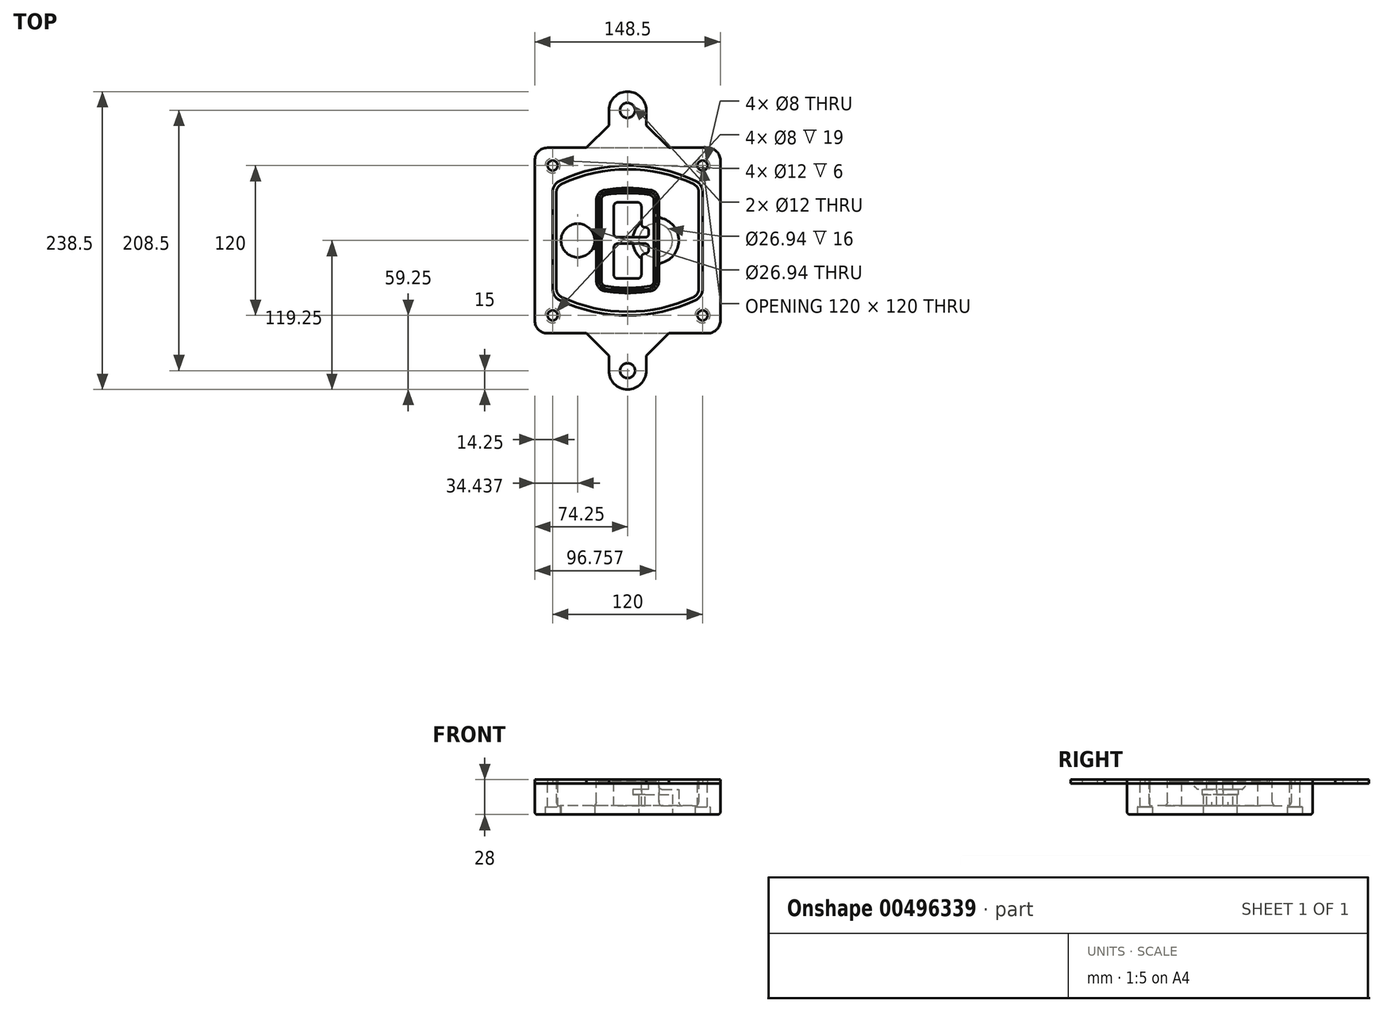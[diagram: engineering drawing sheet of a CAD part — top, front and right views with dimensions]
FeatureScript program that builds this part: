
annotation { "Feature Type Name" : "Feature", "Feature Type Description" : "" }
export const myFeature = defineFeature(function(context is Context, id is Id, definition is map)
    precondition{}
    {
        {
            var Q0;
            Q0=qCreatedBy(makeId("Top.planeOp"),FACE);
            var sketch = newSketch(context, id + "F0", { "sketchPlane" : qUnion([Q0])});
            skPoint(sketch, "E0.rect.middle", {"position": v(0, 0) * mm});
            skLineSegment(sketch, "E1.bottom", {"start": v(-64.25, -74.25) * mm, "end": v(64.25, -74.25) * mm});
            skLineSegment(sketch, "E1.top", {"start": v(-64.25, 74.25) * mm, "end": v(64.25, 74.25) * mm});
            skLineSegment(sketch, "E1.left", {"start": v(-74.25, -64.25) * mm, "end": v(-74.25, 64.25) * mm});
            skLineSegment(sketch, "E1.right", {"start": v(74.25, -64.25) * mm, "end": v(74.25, 64.25) * mm});
            skLineSegment(sketch, "E2", {"start": v(-74.25, 74.25) * mm, "end": v(74.25, -74.25) * mm, "construction": true});
            skLineSegment(sketch, "E3", {"start": v(74.25, 74.25) * mm, "end": v(-74.25, -74.25) * mm, "construction": true});
            skCircle(sketch, "E4", {"center": v(-60, 60) * mm, "radius": 4 * mm});
            skCircle(sketch, "E5", {"center": v(60, 60) * mm, "radius": 4 * mm});
            skCircle(sketch, "E6", {"center": v(60, -60) * mm, "radius": 4 * mm});
            skCircle(sketch, "E7", {"center": v(-60, -60) * mm, "radius": 4 * mm});
            skLineSegment(sketch, "E8", {"start": v(-60, 60) * mm, "end": v(60, 60) * mm, "construction": true});
            skLineSegment(sketch, "E9", {"start": v(60, 60) * mm, "end": v(60, -60) * mm, "construction": true});
            skLineSegment(sketch, "E10", {"start": v(60, -60) * mm, "end": v(-60, -60) * mm, "construction": true});
            skLineSegment(sketch, "E11", {"start": v(-60, -60) * mm, "end": v(-60, 60) * mm, "construction": true});
            skLineSegment(sketch, "E12", {"start": v(-60, 38.83) * mm, "end": v(-60, -38.83) * mm});
            skLineSegment(sketch, "E13", {"start": v(60, 38.83) * mm, "end": v(60, -38.83) * mm});
            skArc(sketch, "E14", {"start": v(54.26, 47.88) * mm, "mid": v(0, 60) * mm, "end": v(-54.26, 47.88) * mm});
            skArc(sketch, "E15", {"start": v(-54.26, -47.88) * mm, "mid": v(0, -60) * mm, "end": v(54.26, -47.88) * mm});
            skLineSegment(sketch, "E16", {"start": v(-60, 0) * mm, "end": v(60, 0) * mm, "construction": true});
            skPoint(sketch, "E17.visualSharp", {"position": v(-60, -45) * mm});
            skArc(sketch, "E17.filletArc", {"start": v(-60, -38.83) * mm, "mid": v(-58.44, -44.2) * mm, "end": v(-54.26, -47.88) * mm});
            skPoint(sketch, "E18.visualSharp", {"position": v(-60, 45) * mm});
            skArc(sketch, "E18.filletArc", {"start": v(-54.26, 47.88) * mm, "mid": v(-58.44, 44.2) * mm, "end": v(-60, 38.83) * mm});
            skPoint(sketch, "E19.visualSharp", {"position": v(60, 45) * mm});
            skArc(sketch, "E19.filletArc", {"start": v(60, 38.83) * mm, "mid": v(58.44, 44.2) * mm, "end": v(54.26, 47.88) * mm});
            skPoint(sketch, "E20.visualSharp", {"position": v(60, -45) * mm});
            skArc(sketch, "E20.filletArc", {"start": v(54.26, -47.88) * mm, "mid": v(58.44, -44.2) * mm, "end": v(60, -38.83) * mm});
            skPoint(sketch, "E21.visualSharp", {"position": v(-74.25, 74.25) * mm});
            skArc(sketch, "E21.filletArc", {"start": v(-64.25, 74.25) * mm, "mid": v(-71.32, 71.32) * mm, "end": v(-74.25, 64.25) * mm});
            skPoint(sketch, "E22.visualSharp", {"position": v(74.25, 74.25) * mm});
            skArc(sketch, "E22.filletArc", {"start": v(74.25, 64.25) * mm, "mid": v(71.32, 71.32) * mm, "end": v(64.25, 74.25) * mm});
            skPoint(sketch, "E23.visualSharp", {"position": v(74.25, -74.25) * mm});
            skArc(sketch, "E23.filletArc", {"start": v(64.25, -74.25) * mm, "mid": v(71.32, -71.32) * mm, "end": v(74.25, -64.25) * mm});
            skPoint(sketch, "E24.visualSharp", {"position": v(-74.25, -74.25) * mm});
            skArc(sketch, "E24.filletArc", {"start": v(-74.25, -64.25) * mm, "mid": v(-71.32, -71.32) * mm, "end": v(-64.25, -74.25) * mm});
            skArc(sketch, "E25.0", {"start": v(57, 38.83) * mm, "mid": v(55.9, 42.58) * mm, "end": v(52.98, 45.17) * mm});
            skLineSegment(sketch, "E25.1", {"start": v(57, 38.83) * mm, "end": v(57, -38.83) * mm});
            skArc(sketch, "E25.2", {"start": v(52.98, -45.17) * mm, "mid": v(55.9, -42.58) * mm, "end": v(57, -38.83) * mm});
            skArc(sketch, "E25.3", {"start": v(-52.98, -45.17) * mm, "mid": v(0, -57) * mm, "end": v(52.98, -45.17) * mm});
            skArc(sketch, "E25.4", {"start": v(-57, -38.83) * mm, "mid": v(-55.9, -42.58) * mm, "end": v(-52.98, -45.17) * mm});
            skArc(sketch, "E25.5", {"start": v(52.98, 45.17) * mm, "mid": v(0, 57) * mm, "end": v(-52.98, 45.17) * mm});
            skLineSegment(sketch, "E25.6", {"start": v(-57, 38.83) * mm, "end": v(-57, -38.83) * mm});
            skArc(sketch, "E25.7", {"start": v(-52.98, 45.17) * mm, "mid": v(-55.9, 42.58) * mm, "end": v(-57, 38.83) * mm});
            skArc(sketch, "E26.0", {"start": v(-55.96, 51.5) * mm, "mid": v(-61.82, 46.33) * mm, "end": v(-64, 38.83) * mm});
            skArc(sketch, "E26.1", {"start": v(55.96, 51.5) * mm, "mid": v(0, 64) * mm, "end": v(-55.96, 51.5) * mm});
            skArc(sketch, "E26.2", {"start": v(64, 38.83) * mm, "mid": v(61.82, 46.33) * mm, "end": v(55.96, 51.5) * mm});
            skLineSegment(sketch, "E26.3", {"start": v(64, 38.83) * mm, "end": v(64, -38.83) * mm});
            skArc(sketch, "E26.4", {"start": v(55.96, -51.5) * mm, "mid": v(61.82, -46.33) * mm, "end": v(64, -38.83) * mm});
            skLineSegment(sketch, "E26.5", {"start": v(-64, 38.83) * mm, "end": v(-64, -38.83) * mm});
            skArc(sketch, "E26.6", {"start": v(-55.96, -51.5) * mm, "mid": v(0, -64) * mm, "end": v(55.96, -51.5) * mm});
            skArc(sketch, "E26.7", {"start": v(-64, -38.83) * mm, "mid": v(-61.82, -46.33) * mm, "end": v(-55.96, -51.5) * mm});
            skSolve(sketch);
        }
        {
            var Q0;
            Q0=makeQuery(id+"F0.imprint","IMPRINT",FACE,{"disambiguationData":[TD([[makeQuery(id+"F0.imprint","IMPRINT",EDGE,{"derivedFrom":sQuery(id+"F0.wireOp",EDGE,"E1.bottom")}),1.0]])]});
            var Q1;
            Q1=makeQuery(id+"F0.imprint","IMPRINT",FACE,{"disambiguationData":[TD([[makeQuery(id+"F0.imprint","IMPRINT",EDGE,{"derivedFrom":sQuery(id+"F0.wireOp",EDGE,"E12")}),1.0]])]});
            var Q2;
            Q2=makeQuery(id+"F0.imprint","IMPRINT",FACE,{"disambiguationData":[TD([[makeQuery(id+"F0.imprint","IMPRINT",EDGE,{"derivedFrom":sQuery(id+"F0.wireOp",EDGE,"E25.0")}),1.0]])]});
            var Q3;
            Q3=makeQuery(id+"F0.imprint","IMPRINT",FACE,{"disambiguationData":[TD([[makeQuery(id+"F0.imprint","IMPRINT",EDGE,{"derivedFrom":sQuery(id+"F0.wireOp",EDGE,"E12")}),-1.0]])]});
            extrude(context, id + "F1", {"entities" : qUnion([Q0, Q1, Q2, Q3]), "oppositeDirection" : true, "depth" : 25 * mm});
        }
        {
            var Q0;
            Q0=makeQuery(id+"F0.imprint","IMPRINT",FACE,{"disambiguationData":[TD([[makeQuery(id+"F0.imprint","IMPRINT",EDGE,{"derivedFrom":sQuery(id+"F0.wireOp",EDGE,"E12")}),1.0]])]});
            extrude(context, id + "F2", {"entities" : qUnion([Q0]), "operationType" : NewBodyOperationType.ADD, "depth" : 3 * mm});
        }
        {
            var Q0;
            Q0=makeQuery(id+"F0.imprint","IMPRINT",FACE,{"disambiguationData":[TD([[makeQuery(id+"F0.imprint","IMPRINT",EDGE,{"derivedFrom":sQuery(id+"F0.wireOp",EDGE,"E25.0")}),1.0]])]});
            extrude(context, id + "F3", {"entities" : qUnion([Q0]), "operationType" : NewBodyOperationType.REMOVE, "oppositeDirection" : true, "depth" : 18 * mm});
        }
        {
            var Q0;
            Q0=makeQuery(id+"F2.opExtrude","CAP_FACE",FACE,{"disambiguationData":[OSD([sQuery(id+"F0.wireOp",EDGE,"E12"),sQuery(id+"F0.wireOp",EDGE,"E13"),sQuery(id+"F0.wireOp",EDGE,"E14"),sQuery(id+"F0.wireOp",EDGE,"E15"),sQuery(id+"F0.wireOp",EDGE,"E17.filletArc"),sQuery(id+"F0.wireOp",EDGE,"E18.filletArc"),sQuery(id+"F0.wireOp",EDGE,"E19.filletArc"),sQuery(id+"F0.wireOp",EDGE,"E20.filletArc"),sQuery(id+"F0.wireOp",EDGE,"E25.0"),sQuery(id+"F0.wireOp",EDGE,"E25.1"),sQuery(id+"F0.wireOp",EDGE,"E25.2"),sQuery(id+"F0.wireOp",EDGE,"E25.3"),sQuery(id+"F0.wireOp",EDGE,"E25.4"),sQuery(id+"F0.wireOp",EDGE,"E25.5"),sQuery(id+"F0.wireOp",EDGE,"E25.6"),sQuery(id+"F0.wireOp",EDGE,"E25.7")])],"isStart":false});
            var sketch = newSketch(context, id + "F4", { "sketchPlane" : qUnion([Q0])});
            skArc(sketch, "E27.0", {"start": v(-18.34, -40.45) * mm, "mid": v(0, -42) * mm, "end": v(18.34, -40.45) * mm});
            skArc(sketch, "E28.0", {"start": v(18.34, 40.45) * mm, "mid": v(0, 42) * mm, "end": v(-18.34, 40.45) * mm});
            skLineSegment(sketch, "E29", {"start": v(-25, 32.57) * mm, "end": v(-25, -32.57) * mm});
            skLineSegment(sketch, "E30", {"start": v(25, 32.57) * mm, "end": v(25, -32.57) * mm});
            skLineSegment(sketch, "E31", {"start": v(-25, 39.1) * mm, "end": v(25, 39.1) * mm, "construction": true});
            skLineSegment(sketch, "E32", {"start": v(-25, -39.1) * mm, "end": v(25, -39.1) * mm, "construction": true});
            skPoint(sketch, "E33.visualSharp", {"position": v(-25, 39.1) * mm});
            skArc(sketch, "E33.filletArc", {"start": v(-18.34, 40.45) * mm, "mid": v(-23.11, 37.73) * mm, "end": v(-25, 32.57) * mm});
            skPoint(sketch, "E34.visualSharp", {"position": v(25, 39.1) * mm});
            skArc(sketch, "E34.filletArc", {"start": v(25, 32.57) * mm, "mid": v(23.11, 37.73) * mm, "end": v(18.34, 40.45) * mm});
            skPoint(sketch, "E35.visualSharp", {"position": v(25, -39.1) * mm});
            skArc(sketch, "E35.filletArc", {"start": v(18.34, -40.45) * mm, "mid": v(23.11, -37.73) * mm, "end": v(25, -32.57) * mm});
            skPoint(sketch, "E36.visualSharp", {"position": v(-25, -39.1) * mm});
            skArc(sketch, "E36.filletArc", {"start": v(-25, -32.57) * mm, "mid": v(-23.11, -37.73) * mm, "end": v(-18.34, -40.45) * mm});
            skArc(sketch, "E37.0", {"start": v(52.98, 45.17) * mm, "mid": v(0, 57) * mm, "end": v(-52.98, 45.17) * mm});
            skArc(sketch, "E37.1", {"start": v(-52.98, 45.17) * mm, "mid": v(-55.9, 42.58) * mm, "end": v(-57, 38.83) * mm});
            skLineSegment(sketch, "E37.2", {"start": v(-57, 38.83) * mm, "end": v(-57, -38.83) * mm});
            skArc(sketch, "E37.3", {"start": v(-57, -38.83) * mm, "mid": v(-55.9, -42.58) * mm, "end": v(-52.98, -45.17) * mm});
            skArc(sketch, "E37.4", {"start": v(-52.98, -45.17) * mm, "mid": v(0, -57) * mm, "end": v(52.98, -45.17) * mm});
            skArc(sketch, "E37.5", {"start": v(52.98, -45.17) * mm, "mid": v(55.9, -42.58) * mm, "end": v(57, -38.83) * mm});
            skLineSegment(sketch, "E37.6", {"start": v(57, 38.83) * mm, "end": v(57, -38.83) * mm});
            skArc(sketch, "E37.7", {"start": v(57, 38.83) * mm, "mid": v(55.9, 42.58) * mm, "end": v(52.98, 45.17) * mm});
            skLineSegment(sketch, "E38.0", {"start": v(23, 32.57) * mm, "end": v(23, -32.57) * mm});
            skArc(sketch, "E38.1", {"start": v(18, -38.48) * mm, "mid": v(21.58, -36.44) * mm, "end": v(23, -32.57) * mm});
            skArc(sketch, "E38.2", {"start": v(-18, -38.48) * mm, "mid": v(0, -40) * mm, "end": v(18, -38.48) * mm});
            skArc(sketch, "E38.3", {"start": v(-23, -32.57) * mm, "mid": v(-21.58, -36.44) * mm, "end": v(-18, -38.48) * mm});
            skLineSegment(sketch, "E38.4", {"start": v(-23, 32.57) * mm, "end": v(-23, -32.57) * mm});
            skArc(sketch, "E38.5", {"start": v(23, 32.57) * mm, "mid": v(21.58, 36.44) * mm, "end": v(18, 38.48) * mm});
            skArc(sketch, "E38.6", {"start": v(-18, 38.48) * mm, "mid": v(-21.58, 36.44) * mm, "end": v(-23, 32.57) * mm});
            skArc(sketch, "E38.7", {"start": v(18, 38.48) * mm, "mid": v(0, 40) * mm, "end": v(-18, 38.48) * mm});
            skArc(sketch, "E39.0", {"start": v(21, 32.57) * mm, "mid": v(20.06, 35.15) * mm, "end": v(17.67, 36.5) * mm});
            skLineSegment(sketch, "E39.1", {"start": v(21, 32.57) * mm, "end": v(21, -32.57) * mm});
            skArc(sketch, "E39.2", {"start": v(17.67, -36.5) * mm, "mid": v(20.06, -35.15) * mm, "end": v(21, -32.57) * mm});
            skArc(sketch, "E39.3", {"start": v(-17.67, -36.5) * mm, "mid": v(0, -38) * mm, "end": v(17.67, -36.5) * mm});
            skArc(sketch, "E39.4", {"start": v(-21, -32.57) * mm, "mid": v(-20.06, -35.15) * mm, "end": v(-17.67, -36.5) * mm});
            skArc(sketch, "E39.5", {"start": v(17.67, 36.5) * mm, "mid": v(0, 38) * mm, "end": v(-17.67, 36.5) * mm});
            skLineSegment(sketch, "E39.6", {"start": v(-21, 32.57) * mm, "end": v(-21, -32.57) * mm});
            skArc(sketch, "E39.7", {"start": v(-17.67, 36.5) * mm, "mid": v(-20.06, 35.15) * mm, "end": v(-21, 32.57) * mm});
            skLineSegment(sketch, "E40", {"start": v(-25, 0) * mm, "end": v(25, 0) * mm, "construction": true});
            skLineSegment(sketch, "E41", {"start": v(-11, 5.5) * mm, "end": v(-11, 27.5) * mm});
            skLineSegment(sketch, "E42", {"start": v(-8, 30.5) * mm, "end": v(8, 30.5) * mm});
            skLineSegment(sketch, "E43", {"start": v(11, 27.5) * mm, "end": v(11, 13.5) * mm});
            skLineSegment(sketch, "E44", {"start": v(14, 10.5) * mm, "end": v(14, 10.5) * mm});
            skLineSegment(sketch, "E45", {"start": v(17, 7.5) * mm, "end": v(17, 5.5) * mm});
            skLineSegment(sketch, "E46", {"start": v(14, 2.5) * mm, "end": v(-8, 2.5) * mm});
            skPoint(sketch, "E47.visualSharp", {"position": v(-11, 30.5) * mm});
            skArc(sketch, "E47.filletArc", {"start": v(-8, 30.5) * mm, "mid": v(-10.12, 29.62) * mm, "end": v(-11, 27.5) * mm});
            skPoint(sketch, "E48.visualSharp", {"position": v(11, 30.5) * mm});
            skArc(sketch, "E48.filletArc", {"start": v(11, 27.5) * mm, "mid": v(10.12, 29.62) * mm, "end": v(8, 30.5) * mm});
            skPoint(sketch, "E49.visualSharp", {"position": v(11, 10.5) * mm});
            skArc(sketch, "E49.filletArc", {"start": v(11, 13.5) * mm, "mid": v(11.88, 11.38) * mm, "end": v(14, 10.5) * mm});
            skPoint(sketch, "E50.visualSharp", {"position": v(17, 10.5) * mm});
            skArc(sketch, "E50.filletArc", {"start": v(17, 7.5) * mm, "mid": v(16.12, 9.62) * mm, "end": v(14, 10.5) * mm});
            skPoint(sketch, "E51.visualSharp", {"position": v(17, 2.5) * mm});
            skArc(sketch, "E51.filletArc", {"start": v(14, 2.5) * mm, "mid": v(16.12, 3.38) * mm, "end": v(17, 5.5) * mm});
            skPoint(sketch, "E52.visualSharp", {"position": v(-11, 2.5) * mm});
            skArc(sketch, "E52.filletArc", {"start": v(-11, 5.5) * mm, "mid": v(-10.12, 3.38) * mm, "end": v(-8, 2.5) * mm});
            skLineSegment(sketch, "E53.0.MirrorCS", {"start": v(14, -2.5) * mm, "end": v(-8, -2.5) * mm});
            skArc(sketch, "E54.0.MirrorCS", {"start": v(-11, -5.5) * mm, "mid": v(-10.12, -3.38) * mm, "end": v(-8, -2.5) * mm});
            skLineSegment(sketch, "E55.0.MirrorCS", {"start": v(-11, -5.5) * mm, "end": v(-11, -27.5) * mm});
            skArc(sketch, "E56.0.MirrorCS", {"start": v(-8, -30.5) * mm, "mid": v(-10.12, -29.62) * mm, "end": v(-11, -27.5) * mm});
            skLineSegment(sketch, "E57.0.MirrorCS", {"start": v(-8, -30.5) * mm, "end": v(8, -30.5) * mm});
            skArc(sketch, "E58.0.MirrorCS", {"start": v(11, -27.5) * mm, "mid": v(10.12, -29.62) * mm, "end": v(8, -30.5) * mm});
            skLineSegment(sketch, "E59.0.MirrorCS", {"start": v(11, -27.5) * mm, "end": v(11, -13.5) * mm});
            skArc(sketch, "E60.0.MirrorCS", {"start": v(11, -13.5) * mm, "mid": v(11.88, -11.38) * mm, "end": v(14, -10.5) * mm});
            skArc(sketch, "E61.0.MirrorCS", {"start": v(17, -7.5) * mm, "mid": v(16.12, -9.62) * mm, "end": v(14, -10.5) * mm});
            skLineSegment(sketch, "E62.0.MirrorCS", {"start": v(17, -7.5) * mm, "end": v(17, -5.5) * mm});
            skArc(sketch, "E63.0.MirrorCS", {"start": v(14, -2.5) * mm, "mid": v(16.12, -3.38) * mm, "end": v(17, -5.5) * mm});
            skSolve(sketch);
        }
        {
            var Q0;
            Q0=makeQuery(id+"F4.imprint","IMPRINT",FACE,{"disambiguationData":[TD([[makeQuery(id+"F4.imprint","IMPRINT",EDGE,{"derivedFrom":sQuery(id+"F4.wireOp",EDGE,"E27.0")}),1.0]])]});
            var Q1;
            Q1=makeQuery(id+"F4.imprint","IMPRINT",FACE,{"disambiguationData":[TD([[makeQuery(id+"F4.imprint","IMPRINT",EDGE,{"derivedFrom":sQuery(id+"F4.wireOp",EDGE,"E38.0")}),-1.0]])]});
            var Q2;
            Q2=makeQuery(id+"F4.imprint","IMPRINT",FACE,{"disambiguationData":[TD([[makeQuery(id+"F4.imprint","IMPRINT",EDGE,{"derivedFrom":sQuery(id+"F4.wireOp",EDGE,"E39.0")}),1.0]])]});
            extrude(context, id + "F5", {"entities" : qUnion([Q0, Q1, Q2]), "operationType" : NewBodyOperationType.ADD, "endBound" : BoundingType.UP_TO_NEXT, "oppositeDirection" : true, "depth" : 25 * mm});
        }
        {
            var Q0;
            Q0=makeQuery(id+"F4.imprint","IMPRINT",FACE,{"disambiguationData":[TD([[makeQuery(id+"F4.imprint","IMPRINT",EDGE,{"derivedFrom":sQuery(id+"F4.wireOp",EDGE,"E38.0")}),-1.0]])]});
            extrude(context, id + "F6", {"entities" : qUnion([Q0]), "operationType" : NewBodyOperationType.REMOVE, "oppositeDirection" : true, "depth" : 2 * mm});
        }
        {
            var Q0;
            Q0=makeQuery(id+"F1.opExtrude","CAP_FACE",FACE,{"disambiguationData":[OSD([sQuery(id+"F0.wireOp",EDGE,"E1.bottom"),sQuery(id+"F0.wireOp",EDGE,"E1.top"),sQuery(id+"F0.wireOp",EDGE,"E1.left"),sQuery(id+"F0.wireOp",EDGE,"E1.right"),sQuery(id+"F0.wireOp",EDGE,"E4"),sQuery(id+"F0.wireOp",EDGE,"E5"),sQuery(id+"F0.wireOp",EDGE,"E6"),sQuery(id+"F0.wireOp",EDGE,"E7"),sQuery(id+"F0.wireOp",EDGE,"E21.filletArc"),sQuery(id+"F0.wireOp",EDGE,"E22.filletArc"),sQuery(id+"F0.wireOp",EDGE,"E23.filletArc"),sQuery(id+"F0.wireOp",EDGE,"E24.filletArc")])],"isStart":false});
            var sketch = newSketch(context, id + "F7", { "sketchPlane" : qUnion([Q0])});
            skCircle(sketch, "E64", {"center": v(22.5, 0) * mm, "radius": 13.47 * mm});
            skCircle(sketch, "E65", {"center": v(-39.81, 0) * mm, "radius": 13.47 * mm});
            skLineSegment(sketch, "E66", {"start": v(74.25, 0) * mm, "end": v(-74.25, 0) * mm});
            skCircle(sketch, "E67", {"center": v(22.5, 0) * mm, "radius": 18.47 * mm});
            skCircle(sketch, "E68", {"center": v(60, -60) * mm, "radius": 6 * mm});
            skCircle(sketch, "E69", {"center": v(-60, -60) * mm, "radius": 6 * mm});
            skCircle(sketch, "E70", {"center": v(-60, 60) * mm, "radius": 6 * mm});
            skCircle(sketch, "E71", {"center": v(60, 60) * mm, "radius": 6 * mm});
            skSolve(sketch);
        }
        {
            var Q0;
            {var subQ1=sQuery(id+"F7.wireOp",EDGE,"E66");var subQ4=sQuery(id+"F7.wireOp",EDGE,"E64");var subQ6=makeQuery(id+"F7.imprint","INTERSECT",VERTEX,{"disambiguationData":[OD(0.0)],"derivedFrom":[subQ4,subQ1]});Q0=makeQuery(id+"F7.imprint","IMPRINT",FACE,{"disambiguationData":[TD([[makeQuery(id+"F7.imprint","IMPRINT",EDGE,{"disambiguationData":[TD([[subQ6,-1.0]])],"derivedFrom":subQ4}),-1.0]])]});}
            var Q1;
            {var subQ0=sQuery(id+"F7.wireOp",EDGE,"E66");var subQ1=sQuery(id+"F7.wireOp",EDGE,"E64");var subQ3=makeQuery(id+"F7.imprint","INTERSECT",VERTEX,{"disambiguationData":[OD(0.0)],"derivedFrom":[subQ1,subQ0]});Q1=makeQuery(id+"F7.imprint","IMPRINT",FACE,{"disambiguationData":[TD([[makeQuery(id+"F7.imprint","IMPRINT",EDGE,{"disambiguationData":[TD([[subQ3,-1.0]])],"derivedFrom":subQ1}),1.0]])]});}
            var Q2;
            {var subQ0=sQuery(id+"F7.wireOp",EDGE,"E66");var subQ1=sQuery(id+"F7.wireOp",EDGE,"E64");var subQ3=makeQuery(id+"F7.imprint","INTERSECT",VERTEX,{"disambiguationData":[OD(0.0)],"derivedFrom":[subQ1,subQ0]});Q2=makeQuery(id+"F7.imprint","IMPRINT",FACE,{"disambiguationData":[TD([[makeQuery(id+"F7.imprint","IMPRINT",EDGE,{"disambiguationData":[TD([[subQ3,1.0]])],"derivedFrom":subQ1}),1.0]])]});}
            var Q3;
            {var subQ1=sQuery(id+"F7.wireOp",EDGE,"E66");var subQ4=sQuery(id+"F7.wireOp",EDGE,"E64");var subQ6=makeQuery(id+"F7.imprint","INTERSECT",VERTEX,{"disambiguationData":[OD(0.0)],"derivedFrom":[subQ4,subQ1]});Q3=makeQuery(id+"F7.imprint","IMPRINT",FACE,{"disambiguationData":[TD([[makeQuery(id+"F7.imprint","IMPRINT",EDGE,{"disambiguationData":[TD([[subQ6,1.0]])],"derivedFrom":subQ4}),-1.0]])]});}
            extrude(context, id + "F8", {"entities" : qUnion([Q0, Q1, Q2, Q3]), "operationType" : NewBodyOperationType.ADD, "oppositeDirection" : true, "depth" : 20 * mm});
        }
        {
            var Q0;
            {var subQ0=sQuery(id+"F7.wireOp",EDGE,"E66");var subQ1=sQuery(id+"F7.wireOp",EDGE,"E64");var subQ3=makeQuery(id+"F7.imprint","INTERSECT",VERTEX,{"disambiguationData":[OD(0.0)],"derivedFrom":[subQ1,subQ0]});Q0=makeQuery(id+"F7.imprint","IMPRINT",FACE,{"disambiguationData":[TD([[makeQuery(id+"F7.imprint","IMPRINT",EDGE,{"disambiguationData":[TD([[subQ3,-1.0]])],"derivedFrom":subQ1}),1.0]])]});}
            var Q1;
            {var subQ0=sQuery(id+"F7.wireOp",EDGE,"E66");var subQ1=sQuery(id+"F7.wireOp",EDGE,"E64");var subQ3=makeQuery(id+"F7.imprint","INTERSECT",VERTEX,{"disambiguationData":[OD(0.0)],"derivedFrom":[subQ1,subQ0]});Q1=makeQuery(id+"F7.imprint","IMPRINT",FACE,{"disambiguationData":[TD([[makeQuery(id+"F7.imprint","IMPRINT",EDGE,{"disambiguationData":[TD([[subQ3,1.0]])],"derivedFrom":subQ1}),1.0]])]});}
            extrude(context, id + "F9", {"entities" : qUnion([Q0, Q1]), "operationType" : NewBodyOperationType.REMOVE, "oppositeDirection" : true, "depth" : 16 * mm});
        }
        {
            var Q0;
            {var subQ0=sQuery(id+"F7.wireOp",EDGE,"E66");var subQ1=sQuery(id+"F7.wireOp",EDGE,"E65");var subQ3=makeQuery(id+"F7.imprint","INTERSECT",VERTEX,{"disambiguationData":[OD(0.0)],"derivedFrom":[subQ1,subQ0]});Q0=makeQuery(id+"F7.imprint","IMPRINT",FACE,{"disambiguationData":[TD([[makeQuery(id+"F7.imprint","IMPRINT",EDGE,{"disambiguationData":[TD([[subQ3,-1.0]])],"derivedFrom":subQ1}),1.0]])]});}
            var Q1;
            {var subQ0=sQuery(id+"F7.wireOp",EDGE,"E66");var subQ1=sQuery(id+"F7.wireOp",EDGE,"E65");var subQ3=makeQuery(id+"F7.imprint","INTERSECT",VERTEX,{"disambiguationData":[OD(0.0)],"derivedFrom":[subQ1,subQ0]});Q1=makeQuery(id+"F7.imprint","IMPRINT",FACE,{"disambiguationData":[TD([[makeQuery(id+"F7.imprint","IMPRINT",EDGE,{"disambiguationData":[TD([[subQ3,1.0]])],"derivedFrom":subQ1}),1.0]])]});}
            extrude(context, id + "F10", {"entities" : qUnion([Q0, Q1]), "operationType" : NewBodyOperationType.REMOVE, "oppositeDirection" : true, "depth" : 25 * mm});
        }
        {
            var Q0;
            Q0=makeQuery(id+"F7.imprint","IMPRINT",FACE,{"disambiguationData":[TD([[makeQuery(id+"F7.imprint","IMPRINT",EDGE,{"derivedFrom":sQuery(id+"F7.wireOp",EDGE,"E68")}),1.0]])]});
            var Q1;
            Q1=makeQuery(id+"F7.imprint","IMPRINT",FACE,{"disambiguationData":[TD([[makeQuery(id+"F7.imprint","IMPRINT",EDGE,{"derivedFrom":makeQuery(id+"F1.opExtrude","CAP_EDGE",EDGE,{"disambiguationData":[OSD([sQuery(id+"F0.wireOp",EDGE,"E5")])],"isStart":false})}),-1.0]])]});
            var Q2;
            Q2=makeQuery(id+"F7.imprint","IMPRINT",FACE,{"disambiguationData":[TD([[makeQuery(id+"F7.imprint","IMPRINT",EDGE,{"derivedFrom":sQuery(id+"F7.wireOp",EDGE,"E69")}),1.0]])]});
            var Q3;
            Q3=makeQuery(id+"F7.imprint","IMPRINT",FACE,{"disambiguationData":[TD([[makeQuery(id+"F7.imprint","IMPRINT",EDGE,{"derivedFrom":makeQuery(id+"F1.opExtrude","CAP_EDGE",EDGE,{"disambiguationData":[OSD([sQuery(id+"F0.wireOp",EDGE,"E4")])],"isStart":false})}),-1.0]])]});
            var Q4;
            Q4=makeQuery(id+"F7.imprint","IMPRINT",FACE,{"disambiguationData":[TD([[makeQuery(id+"F7.imprint","IMPRINT",EDGE,{"derivedFrom":sQuery(id+"F7.wireOp",EDGE,"E70")}),1.0]])]});
            var Q5;
            Q5=makeQuery(id+"F7.imprint","IMPRINT",FACE,{"disambiguationData":[TD([[makeQuery(id+"F7.imprint","IMPRINT",EDGE,{"derivedFrom":makeQuery(id+"F1.opExtrude","CAP_EDGE",EDGE,{"disambiguationData":[OSD([sQuery(id+"F0.wireOp",EDGE,"E7")])],"isStart":false})}),-1.0]])]});
            var Q6;
            Q6=makeQuery(id+"F7.imprint","IMPRINT",FACE,{"disambiguationData":[TD([[makeQuery(id+"F7.imprint","IMPRINT",EDGE,{"derivedFrom":sQuery(id+"F7.wireOp",EDGE,"E71")}),1.0]])]});
            var Q7;
            Q7=makeQuery(id+"F7.imprint","IMPRINT",FACE,{"disambiguationData":[TD([[makeQuery(id+"F7.imprint","IMPRINT",EDGE,{"derivedFrom":makeQuery(id+"F1.opExtrude","CAP_EDGE",EDGE,{"disambiguationData":[OSD([sQuery(id+"F0.wireOp",EDGE,"E6")])],"isStart":false})}),-1.0]])]});
            extrude(context, id + "F11", {"entities" : qUnion([Q0, Q1, Q2, Q3, Q4, Q5, Q6, Q7]), "operationType" : NewBodyOperationType.REMOVE, "oppositeDirection" : true, "depth" : 6 * mm});
        }
        {
            var Q0;
            Q0=makeQuery(id+"F9.boolean.opBoolean","COPY",FACE,{"derivedFrom":makeQuery(id+"F9.opExtrude","CAP_FACE",FACE,{"disambiguationData":[OSD([sQuery(id+"F7.wireOp",EDGE,"E64")])],"isStart":false})});
            var sketch = newSketch(context, id + "F12", { "sketchPlane" : qUnion([Q0])});
            skArc(sketch, "E72.0", {"start": v(11, 14.45) * mm, "mid": v(6.45, 9.13) * mm, "end": v(4.2, 2.5) * mm});
            skArc(sketch, "E72.1", {"start": v(4.2, -2.5) * mm, "mid": v(6.45, -9.13) * mm, "end": v(11, -14.45) * mm});
            skLineSegment(sketch, "E73", {"start": v(4.2, -2.5) * mm, "end": v(14, -2.5) * mm});
            skLineSegment(sketch, "E74.0", {"start": v(14, 2.5) * mm, "end": v(4.2, 2.5) * mm});
            skArc(sketch, "E74.1", {"start": v(14, 2.5) * mm, "mid": v(16.12, 3.38) * mm, "end": v(17, 5.5) * mm});
            skLineSegment(sketch, "E74.2", {"start": v(17, 7.5) * mm, "end": v(17, 5.5) * mm});
            skArc(sketch, "E74.3", {"start": v(17, 7.5) * mm, "mid": v(16.12, 9.62) * mm, "end": v(14, 10.5) * mm});
            skArc(sketch, "E74.4", {"start": v(11, 13.5) * mm, "mid": v(11.88, 11.38) * mm, "end": v(14, 10.5) * mm});
            skLineSegment(sketch, "E74.5", {"start": v(11, 14.45) * mm, "end": v(11, 13.5) * mm});
            skLineSegment(sketch, "E74.7", {"start": v(14, -2.5) * mm, "end": v(4.2, -2.5) * mm});
            skArc(sketch, "E74.8", {"start": v(14, -2.5) * mm, "mid": v(16.12, -3.38) * mm, "end": v(17, -5.5) * mm});
            skLineSegment(sketch, "E74.9", {"start": v(17, -7.5) * mm, "end": v(17, -5.5) * mm});
            skArc(sketch, "E74.10", {"start": v(17, -7.5) * mm, "mid": v(16.12, -9.62) * mm, "end": v(14, -10.5) * mm});
            skArc(sketch, "E74.11", {"start": v(11, -13.5) * mm, "mid": v(11.88, -11.38) * mm, "end": v(14, -10.5) * mm});
            skLineSegment(sketch, "E74.12", {"start": v(11, -14.45) * mm, "end": v(11, -13.5) * mm});
            skPoint(sketch, "E75.orphan", {"position": v(11, -27.5) * mm});
            skPoint(sketch, "E76.orphan", {"position": v(-8, -2.5) * mm});
            skPoint(sketch, "E77.orphan", {"position": v(-8, 2.5) * mm});
            skPoint(sketch, "E78.orphan", {"position": v(11, 27.5) * mm});
            skSolve(sketch);
        }
        {
            var Q0;
            {var subQ7=sQuery(id+"F12.wireOp",EDGE,"E72.0");var subQ14=sQuery(id+"F12.wireOp",EDGE,"E72.1");var subQ16=sQuery(id+"F12.wireOp",EDGE,"E74.1");var subQ18=sQuery(id+"F12.wireOp",EDGE,"E74.8");Q0=qUnion([makeQuery(id+"F12.imprint","IMPRINT",FACE,{"disambiguationData":[TD([[makeQuery(id+"F12.imprint","IMPRINT",EDGE,{"derivedFrom":subQ7}),1.0]])]}),makeQuery(id+"F12.imprint","IMPRINT",FACE,{"disambiguationData":[TD([[makeQuery(id+"F12.imprint","IMPRINT",EDGE,{"derivedFrom":subQ14}),1.0]])]}),makeQuery(id+"F12.imprint","IMPRINT",FACE,{"disambiguationData":[TD([[makeQuery(id+"F12.imprint","IMPRINT",EDGE,{"derivedFrom":subQ16}),1.0]])]}),makeQuery(id+"F12.imprint","IMPRINT",FACE,{"disambiguationData":[TD([[makeQuery(id+"F12.imprint","IMPRINT",EDGE,{"derivedFrom":subQ18}),-1.0]])]})]);}
            var Q1;
            Q1=makeQuery(id+"F5.boolean.opBoolean","SPLIT",FACE,{"disambiguationData":[TD([makeQuery(id+"F5.opExtrude","SWEPT_FACE",FACE,{"disambiguationData":[OSD([sQuery(id+"F4.wireOp",EDGE,"E41")])]})])],"derivedFrom":makeQuery(id+"F3.boolean.opBoolean","COPY",FACE,{"derivedFrom":makeQuery(id+"F3.opExtrude","CAP_FACE",FACE,{"disambiguationData":[OSD([sQuery(id+"F0.wireOp",EDGE,"E25.0"),sQuery(id+"F0.wireOp",EDGE,"E25.1"),sQuery(id+"F0.wireOp",EDGE,"E25.2"),sQuery(id+"F0.wireOp",EDGE,"E25.3"),sQuery(id+"F0.wireOp",EDGE,"E25.4"),sQuery(id+"F0.wireOp",EDGE,"E25.5"),sQuery(id+"F0.wireOp",EDGE,"E25.6"),sQuery(id+"F0.wireOp",EDGE,"E25.7")])],"isStart":false})})});
            extrude(context, id + "F13", {"entities" : qUnion([Q0]), "operationType" : NewBodyOperationType.REMOVE, "endBound" : BoundingType.UP_TO_SURFACE, "endBoundEntityFace" : qUnion([Q1]), "depth" : 25 * mm});
        }
        {
            var Q0;
            Q0=makeQuery(id+"F3.boolean.opBoolean","COPY",EDGE,{"derivedFrom":makeQuery(id+"F3.opExtrude","CAP_EDGE",EDGE,{"disambiguationData":[OSD([sQuery(id+"F0.wireOp",EDGE,"E25.6")])],"isStart":false})});
            var Q1;
            Q1=makeQuery(id+"F8.boolean.opBoolean","INTERSECT",EDGE,{"derivedFrom":[makeQuery(id+"F5.opExtrude","SWEPT_FACE",FACE,{"disambiguationData":[OSD([sQuery(id+"F4.wireOp",EDGE,"E30")])]}),makeQuery(id+"F8.opExtrude","CAP_FACE",FACE,{"disambiguationData":[OSD([sQuery(id+"F7.wireOp",EDGE,"E67")])],"isStart":false})]});
            var Q2;
            Q2=makeQuery(id+"F8.boolean.opBoolean","INTERSECT",EDGE,{"disambiguationData":[OD(1.0)],"derivedFrom":[makeQuery(id+"F5.opExtrude","SWEPT_FACE",FACE,{"disambiguationData":[OSD([sQuery(id+"F4.wireOp",EDGE,"E30")])]}),makeQuery(id+"F8.opExtrude","SWEPT_FACE",FACE,{"disambiguationData":[OSD([sQuery(id+"F7.wireOp",EDGE,"E67")])]})]});
            var Q3;
            {var subQ0=sQuery(id+"F4.wireOp",EDGE,"E30");Q3=makeQuery(id+"F8.boolean.opBoolean","SPLIT",EDGE,{"disambiguationData":[TD([makeQuery(id+"F5.opExtrude","SWEPT_FACE",FACE,{"disambiguationData":[OSD([sQuery(id+"F4.wireOp",EDGE,"E35.filletArc")])]})])],"derivedFrom":makeQuery(id+"F5.opExtrude","CAP_EDGE",EDGE,{"disambiguationData":[OSD([subQ0])],"isStart":false})});}
            var Q4;
            {var subQ0=sQuery(id+"F0.wireOp",EDGE,"E25.7");var subQ1=sQuery(id+"F0.wireOp",EDGE,"E25.1");var subQ2=sQuery(id+"F0.wireOp",EDGE,"E25.6");var subQ3=sQuery(id+"F0.wireOp",EDGE,"E25.5");var subQ4=sQuery(id+"F0.wireOp",EDGE,"E25.4");var subQ5=sQuery(id+"F0.wireOp",EDGE,"E25.0");var subQ6=sQuery(id+"F0.wireOp",EDGE,"E25.2");var subQ7=sQuery(id+"F0.wireOp",EDGE,"E25.3");Q4=makeQuery(id+"F8.boolean.opBoolean","INTERSECT",EDGE,{"derivedFrom":[makeQuery(id+"F5.boolean.opBoolean","SPLIT",FACE,{"disambiguationData":[TD([makeQuery(id+"F2.opExtrude","SWEPT_FACE",FACE,{"disambiguationData":[OSD([subQ5])]})])],"derivedFrom":makeQuery(id+"F3.boolean.opBoolean","COPY",FACE,{"derivedFrom":makeQuery(id+"F3.opExtrude","CAP_FACE",FACE,{"disambiguationData":[OSD([subQ5,subQ1,subQ6,subQ7,subQ4,subQ3,subQ2,subQ0])],"isStart":false})})}),makeQuery(id+"F8.opExtrude","SWEPT_FACE",FACE,{"disambiguationData":[OSD([sQuery(id+"F7.wireOp",EDGE,"E67")])]})]});}
            var Q5;
            Q5=makeQuery(id+"F8.boolean.opBoolean","INTERSECT",EDGE,{"disambiguationData":[OD(0.0)],"derivedFrom":[makeQuery(id+"F5.opExtrude","SWEPT_FACE",FACE,{"disambiguationData":[OSD([sQuery(id+"F4.wireOp",EDGE,"E30")])]}),makeQuery(id+"F8.opExtrude","SWEPT_FACE",FACE,{"disambiguationData":[OSD([sQuery(id+"F7.wireOp",EDGE,"E67")])]})]});
            fillet(context, id + "F14", {"entities" : qUnion([Q0, Q1, Q2, Q3, Q4, Q5]), "radius" : 3 * mm, "tangentPropagation" : true, "allowEdgeOverflow" : false});
        }
        {
            var Q0;
            Q0=makeQuery(id+"F1.opExtrude","CAP_EDGE",EDGE,{"disambiguationData":[OSD([sQuery(id+"F0.wireOp",EDGE,"E1.bottom")])],"isStart":false});
            fillet(context, id + "F15", {"entities" : qUnion([Q0]), "radius" : 2 * mm, "tangentPropagation" : true, "allowEdgeOverflow" : false});
        }
        {
            var Q0;
            {var subQ0=sQuery(id+"F0.wireOp",EDGE,"E21.filletArc");var subQ1=sQuery(id+"F0.wireOp",EDGE,"E7");var subQ2=sQuery(id+"F0.wireOp",EDGE,"E6");var subQ3=sQuery(id+"F0.wireOp",EDGE,"E5");var subQ4=sQuery(id+"F0.wireOp",EDGE,"E4");var subQ5=sQuery(id+"F0.wireOp",EDGE,"E22.filletArc");var subQ6=sQuery(id+"F0.wireOp",EDGE,"E1.bottom");var subQ7=sQuery(id+"F0.wireOp",EDGE,"E1.right");var subQ8=sQuery(id+"F0.wireOp",EDGE,"E1.top");var subQ9=sQuery(id+"F0.wireOp",EDGE,"E1.left");var subQ10=sQuery(id+"F0.wireOp",EDGE,"E23.filletArc");var subQ11=sQuery(id+"F0.wireOp",EDGE,"E24.filletArc");Q0=makeQuery(id+"F2.boolean.opBoolean","SPLIT",FACE,{"disambiguationData":[TD([makeQuery(id+"F1.opExtrude","SWEPT_FACE",FACE,{"disambiguationData":[OSD([subQ6])]})])],"derivedFrom":makeQuery(id+"F1.opExtrude","CAP_FACE",FACE,{"disambiguationData":[OSD([subQ6,subQ8,subQ9,subQ7,subQ4,subQ3,subQ2,subQ1,subQ0,subQ5,subQ10,subQ11])],"isStart":true})});}
            var sketch = newSketch(context, id + "F16", { "sketchPlane" : qUnion([Q0])});
            skLineSegment(sketch, "E79", {"start": v(0, 74.25) * mm, "end": v(0, 104.25) * mm, "construction": true});
            skCircle(sketch, "E80", {"center": v(0, 104.25) * mm, "radius": 6 * mm});
            skLineSegment(sketch, "E81", {"start": v(-33, 74.25) * mm, "end": v(-15, 92.25) * mm});
            skLineSegment(sketch, "E82", {"start": v(33, 74.25) * mm, "end": v(15, 92.25) * mm});
            skLineSegment(sketch, "E83", {"start": v(-15, 92.25) * mm, "end": v(-15, 104.25) * mm});
            skLineSegment(sketch, "E84", {"start": v(15, 92.25) * mm, "end": v(15, 104.25) * mm});
            skArc(sketch, "E85", {"start": v(15, 104.25) * mm, "mid": v(0, 119.25) * mm, "end": v(-15, 104.25) * mm});
            skLineSegment(sketch, "E86", {"start": v(-74.25, 0) * mm, "end": v(74.25, 0) * mm, "construction": true});
            skLineSegment(sketch, "E87.MirrorCS", {"start": v(-33, -74.25) * mm, "end": v(-15, -92.25) * mm});
            skLineSegment(sketch, "E88.MirrorCS", {"start": v(-15, -92.25) * mm, "end": v(-15, -104.25) * mm});
            skLineSegment(sketch, "E89.MirrorCS", {"start": v(0, -74.25) * mm, "end": v(0, -104.25) * mm, "construction": true});
            skCircle(sketch, "E90.MirrorC", {"center": v(0, -104.25) * mm, "radius": 6 * mm});
            skLineSegment(sketch, "E91.MirrorCS", {"start": v(15, -92.25) * mm, "end": v(15, -104.25) * mm});
            skLineSegment(sketch, "E92.MirrorCS", {"start": v(33, -74.25) * mm, "end": v(15, -92.25) * mm});
            skArc(sketch, "E93.MirrorCS", {"start": v(15, -104.25) * mm, "mid": v(0, -119.25) * mm, "end": v(-15, -104.25) * mm});
            skSolve(sketch);
        }
        {
            var Q0;
            Q0=makeQuery(id+"F16.imprint","IMPRINT",FACE,{"disambiguationData":[TD([[makeQuery(id+"F16.imprint","IMPRINT",EDGE,{"derivedFrom":makeQuery(id+"F1.opExtrude","CAP_EDGE",EDGE,{"disambiguationData":[OSD([sQuery(id+"F0.wireOp",EDGE,"E1.left")])],"isStart":true})}),-1.0]])]});
            var Q1;
            Q1=makeQuery(id+"F16.imprint","IMPRINT",FACE,{"disambiguationData":[TD([[makeQuery(id+"F16.imprint","IMPRINT",EDGE,{"derivedFrom":sQuery(id+"F16.wireOp",EDGE,"E80")}),-1.0]])]});
            var Q2;
            {var subQ0=sQuery(id+"F16.wireOp",EDGE,"E87.MirrorCS");Q2=makeQuery(id+"F16.imprint","IMPRINT",FACE,{"disambiguationData":[TD([[makeQuery(id+"F16.imprint","IMPRINT",EDGE,{"derivedFrom":subQ0}),1.0]])]});}
            var Q3;
            Q3=makeQuery(id+"F2.opExtrude","CAP_FACE",FACE,{"disambiguationData":[OSD([sQuery(id+"F0.wireOp",EDGE,"E12"),sQuery(id+"F0.wireOp",EDGE,"E13"),sQuery(id+"F0.wireOp",EDGE,"E14"),sQuery(id+"F0.wireOp",EDGE,"E15"),sQuery(id+"F0.wireOp",EDGE,"E17.filletArc"),sQuery(id+"F0.wireOp",EDGE,"E18.filletArc"),sQuery(id+"F0.wireOp",EDGE,"E19.filletArc"),sQuery(id+"F0.wireOp",EDGE,"E20.filletArc"),sQuery(id+"F0.wireOp",EDGE,"E25.0"),sQuery(id+"F0.wireOp",EDGE,"E25.1"),sQuery(id+"F0.wireOp",EDGE,"E25.2"),sQuery(id+"F0.wireOp",EDGE,"E25.3"),sQuery(id+"F0.wireOp",EDGE,"E25.4"),sQuery(id+"F0.wireOp",EDGE,"E25.5"),sQuery(id+"F0.wireOp",EDGE,"E25.6"),sQuery(id+"F0.wireOp",EDGE,"E25.7")])],"isStart":false});
            extrude(context, id + "F17", {"entities" : qUnion([Q0, Q1, Q2]), "endBound" : BoundingType.UP_TO_SURFACE, "endBoundEntityFace" : qUnion([Q3]), "depth" : 25 * mm});
        }
    });
